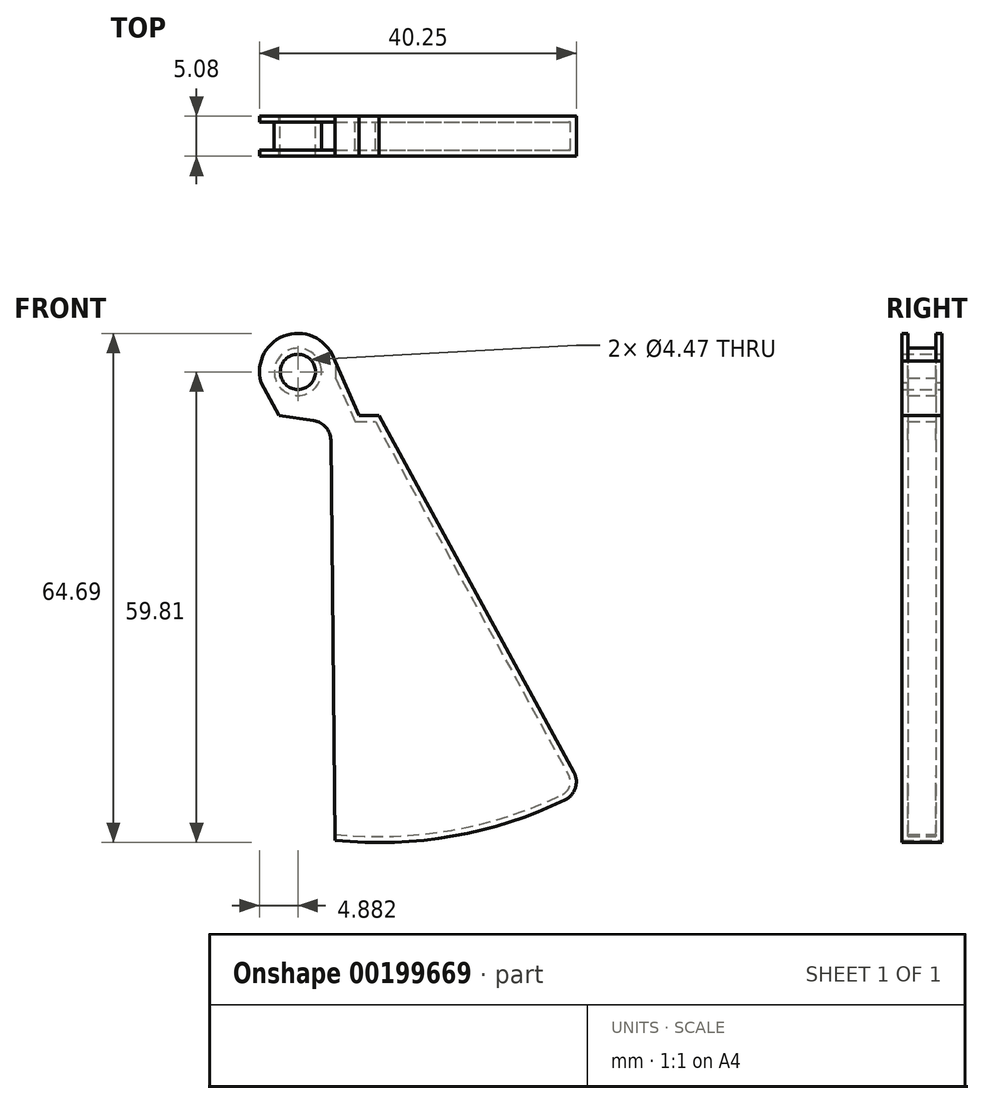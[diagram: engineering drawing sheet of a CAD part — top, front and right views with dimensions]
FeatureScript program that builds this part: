
annotation { "Feature Type Name" : "Feature", "Feature Type Description" : "" }
export const myFeature = defineFeature(function(context is Context, id is Id, definition is map)
    precondition{}
    {
        {
            var Q0;
            Q0=qCreatedBy(makeId("Front.planeOp"),FACE);
            var sketch = newSketch(context, id + "F0", { "sketchPlane" : qUnion([Q0])});
            skLineSegment(sketch, "E0", {"start": v(5.55, 53.98) * mm, "end": v(30.31, 8.64) * mm});
            skArc(sketch, "E1", {"start": v(0, 0) * mm, "mid": v(14.95, 0.54) * mm, "end": v(29.2, 5.13) * mm});
            skPoint(sketch, "E2.visualSharp", {"position": v(31.56, 6.35) * mm});
            skArc(sketch, "E2.filletArc", {"start": v(29.2, 5.13) * mm, "mid": v(30.5, 6.64) * mm, "end": v(30.31, 8.64) * mm});
            skArc(sketch, "E3", {"start": v(-0.06, 60.87) * mm, "mid": v(-6.1, 64.2) * mm, "end": v(-9.44, 58.17) * mm});
            skLineSegment(sketch, "E4", {"start": v(-0.06, 60.87) * mm, "end": v(3.01, 53.98) * mm});
            skLineSegment(sketch, "E5", {"start": v(3.01, 53.98) * mm, "end": v(5.55, 53.98) * mm});
            skLineSegment(sketch, "E6", {"start": v(-9.44, 58.17) * mm, "end": v(-7.15, 53.97) * mm});
            skLineSegment(sketch, "E7", {"start": v(-7.15, 53.97) * mm, "end": v(-2.73, 53.31) * mm});
            skLineSegment(sketch, "E8", {"start": v(-0.56, 50.83) * mm, "end": v(0, 0) * mm});
            skPoint(sketch, "E9.visualSharp", {"position": v(-0.59, 53) * mm});
            skArc(sketch, "E9.filletArc", {"start": v(-0.56, 50.83) * mm, "mid": v(-1.19, 52.47) * mm, "end": v(-2.73, 53.31) * mm});
            skCircle(sketch, "E10", {"center": v(-4.75, 59.52) * mm, "radius": 2.24 * mm});
            skSolve(sketch);
        }
        {
            var Q0;
            Q0=makeQuery(id+"F0.imprint","IMPRINT",FACE,{"disambiguationData":[TD([[makeQuery(id+"F0.imprint","IMPRINT",EDGE,{"derivedFrom":sQuery(id+"F0.wireOp",EDGE,"E0")}),-1.0]])]});
            extrude(context, id + "F1", {"entities" : qUnion([Q0]), "depth" : 5.08 * mm});
        }
        {
            var Q0;
            Q0=makeQuery(id+"F1.opExtrude","SWEPT_FACE",FACE,{"disambiguationData":[OSD([sQuery(id+"F0.wireOp",EDGE,"E8")])]});
            var Q1;
            Q1=makeQuery(id+"F1.opExtrude","SWEPT_FACE",FACE,{"disambiguationData":[OSD([sQuery(id+"F0.wireOp",EDGE,"E9.filletArc")])]});
            var Q2;
            Q2=makeQuery(id+"F1.opExtrude","SWEPT_FACE",FACE,{"disambiguationData":[OSD([sQuery(id+"F0.wireOp",EDGE,"E7")])]});
            var Q3;
            Q3=makeQuery(id+"F1.opExtrude","SWEPT_FACE",FACE,{"disambiguationData":[OSD([sQuery(id+"F0.wireOp",EDGE,"E6")])]});
            var Q4;
            Q4=makeQuery(id+"F1.opExtrude","SWEPT_FACE",FACE,{"disambiguationData":[OSD([sQuery(id+"F0.wireOp",EDGE,"E3")])]});
            shell(context, id + "F2", {"entities" : qUnion([Q0, Q1, Q2, Q3, Q4]), "thickness" : 0.76 * mm});
        }
        {
            var Q0;
            Q0=makeQuery(id+"F1.opExtrude","SWEPT_BODY",BODY,{"disambiguationData":[OSD([sQuery(id+"F0.wireOp",EDGE,"E0"),sQuery(id+"F0.wireOp",EDGE,"E1"),sQuery(id+"F0.wireOp",EDGE,"E2.filletArc"),sQuery(id+"F0.wireOp",EDGE,"E3"),sQuery(id+"F0.wireOp",EDGE,"E4"),sQuery(id+"F0.wireOp",EDGE,"E5"),sQuery(id+"F0.wireOp",EDGE,"E6"),sQuery(id+"F0.wireOp",EDGE,"E7"),sQuery(id+"F0.wireOp",EDGE,"E8"),sQuery(id+"F0.wireOp",EDGE,"E9.filletArc"),sQuery(id+"F0.wireOp",EDGE,"E10")])]});
            transform(context, id + "F3", {"entities" : qUnion([Q0]), "transformType" : TransformType.TRANSLATION_3D, "dx" : 0 * mm, "dy" : 0 * mm, "dz" : 0 * mm, "makeCopy" : true});
        }
    });
